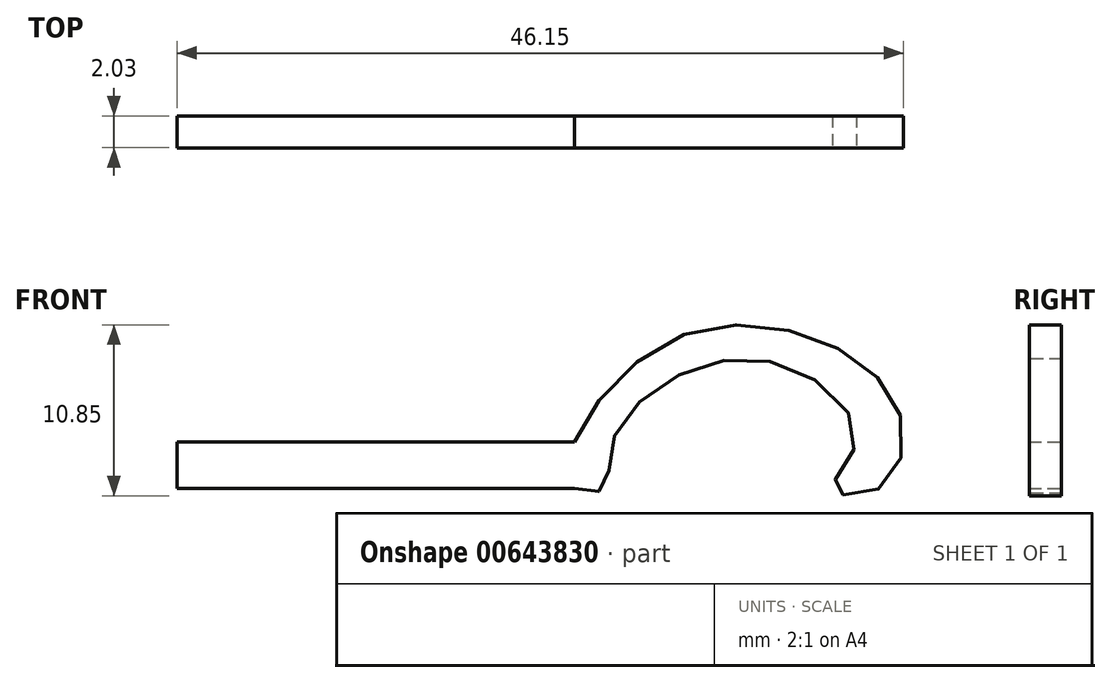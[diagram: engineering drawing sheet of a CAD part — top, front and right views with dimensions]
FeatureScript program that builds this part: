
annotation { "Feature Type Name" : "Feature", "Feature Type Description" : "" }
export const myFeature = defineFeature(function(context is Context, id is Id, definition is map)
    precondition{}
    {
        {
            var Q0;
            Q0=qCreatedBy(makeId("Front.planeOp"),FACE);
            var sketch = newSketch(context, id + "F0", { "sketchPlane" : qUnion([Q0])});
            skLineSegment(sketch, "E0", {"start": v(-68.12, 9.13) * mm, "end": v(-42.86, 9.13) * mm});
            skLineSegment(sketch, "E1", {"start": v(-68.12, 9.13) * mm, "end": v(-68.12, 6.18) * mm});
            skLineSegment(sketch, "E2", {"start": v(-68.12, 6.18) * mm, "end": v(-42.86, 6.18) * mm});
            skLineSegment(sketch, "E3", {"start": v(-42.86, 9.13) * mm, "end": v(-42.86, 6.18) * mm});
            skFitSpline(sketch, "E4", {"points": [v(-42.86, 9.13) * mm, v(-36.78, 15.58) * mm, v(-27.75, 15.76) * mm, v(-22.21, 10.96) * mm, v(-23.5, 6.18) * mm, v(-26.46, 6.18) * mm, v(-24.98, 9.13) * mm, v(-28.85, 13.73) * mm, v(-35.86, 13.55) * mm, v(-40.47, 9.13) * mm, v(-41.02, 6.18) * mm, v(-42.86, 6.18) * mm, v(-42.86, 9.13) * mm]});
            skSolve(sketch);
        }
        {
            var Q0;
            Q0 = qSketchRegion(id + "F0", true);
            extrude(context, id + "F1", {"entities" : qUnion([Q0]), "depth" : 2.03 * mm, "offsetDistance" : 25.4 * mm});
        }
    });
